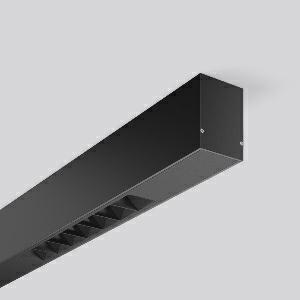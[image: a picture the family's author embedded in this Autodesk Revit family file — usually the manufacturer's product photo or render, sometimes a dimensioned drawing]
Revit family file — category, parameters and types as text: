
# Revit family: less_is_more_beamline_312498_003_76_e99d
name_source: partatom
category: Lighting Fixtures
units: mm (PartAtom-declared; Revit-internal decimal feet)

## family parameters
Cut with Voids When Loaded = No
Host = Face
Light Source = No
Part Type = Normal
Room Calculation Point = No
Round Connector Dimension = Use Diameter
Shared = No

## types (1)
- LESS IS MORE BEAMLINE (1 x LED Modul 930, 1800 lm, 3000)
    Apparent Load = 97 VA
    CIE Flux Codes = 100 100 100 100 100
    Color Rendering = 90
    Color Temperature = 3000
    Default Elevation = 1800 mm  [stored 5.90551 ft]
    Description = Series: LESS IS MORE BEAMLINE
Linear ceiling and wall luminaire for aesthetically sophisticated lighting. Luminaire with four LED light units. Housing: extruded aluminium profile, powder-coated. End cap aluminium powder-coated. LED light unit with MRS technology: Mini-Reflector-System made of metallised thermoplastic with prismatic black glare-suppressing frame for pleasant glare-free light (RUG < 10). Each LED light unit has 7 reflector elements. Narrow beam light distribution. LED unit with integrated converter interchangeable and removable. Suitable for through-wiring. 
Colour: deep black, matt (RAL 9005)
Length: 2248 mm
Width: 57 mm
Height: 75 mm
Lamp: LED
Socket: without socket
Colour temperature: 3000K
Colour rendering index (CRI): 90
System power: 97 W
Rated luminous flux: 7200 lm
Luminous efficiency: 74 lm/W
Control gear: Converter, dimmable, DALI
Protection class: I
Type of protection: IP 20
    Height = 75 mm
    Lamp = 1 x LED Modul 930
    Lamp Light Flux = 1800 lm
    Lamp count = 1
    Length = 2248 mm
    Lifetime = 50000 h
    Luminous efficacy = 74 lm/W
    Manufacturer = RZB
    ModVariant = No
    Model = 312498.003.76
    Mounting Place = Ceiling, Wall
    Mounting Type = Surface mounted
    Number of Poles = 1
    OnlyDefault = Yes
    Power Factor = 1
    Product Name = LESS IS MORE BEAMLINE
    Product group = Surface mounted LED linear luminaires
    ProductGroupID = 307
    Protection Class = Protection class I
    Protection Degree = IP 20
    RLX_Detail_Level = 1
    RLX_Emergency_Light_Flux = 0 lm
    RLX_Emergency_Type = 0
    RLX_Emergency_Type_DB = No
    RlxData = <blob elided: 30469 chars, md5=04d69ed6>
    Socket = socket
    Standby Power = 0 W
    System Light Flux = 7200 lm
    System Power = 97 W
    Type Comments = Product without accessories
    Type Image = 312483.003.jpg
    URL = http://relux.com
    VarID = ---
    Voltage = 230 V
    Voltage Range = 220-240 V
    Weight = 0.00 kg
    Width = 57 mm

note: [stored X ft] marks values corroborated as IEEE doubles in the binary element streams (Revit-internal decimal feet)

## geometry (parser evidence)
native form markers: Blend x4, Sweep x19
no freeform markers — native parametric forms only
